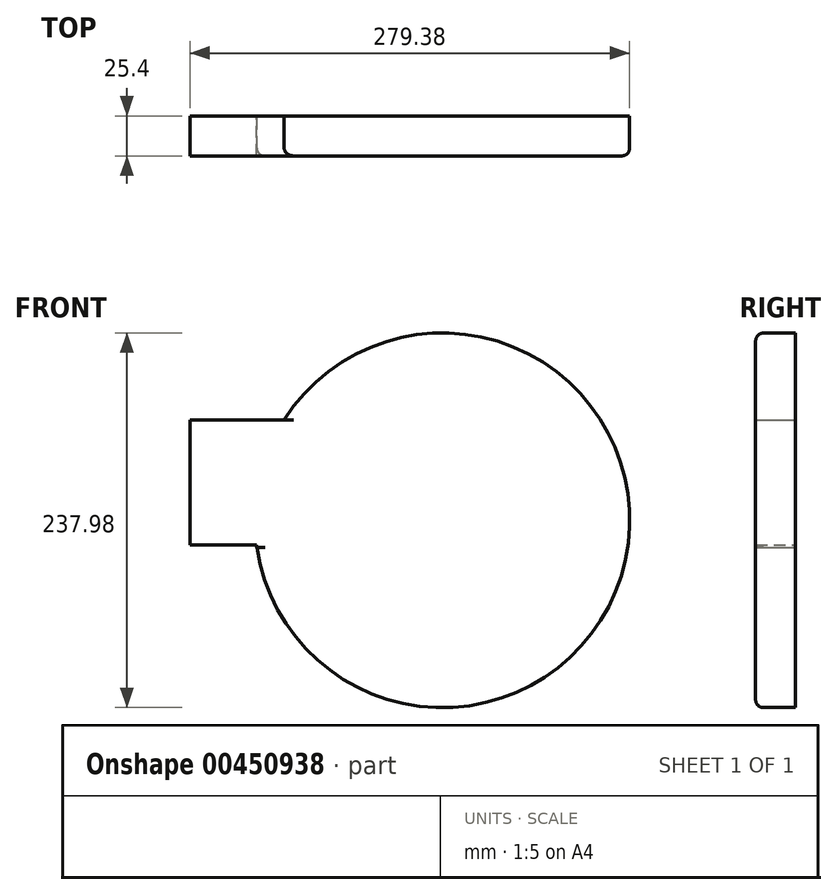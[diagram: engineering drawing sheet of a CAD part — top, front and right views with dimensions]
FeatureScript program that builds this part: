
annotation { "Feature Type Name" : "Feature", "Feature Type Description" : "" }
export const myFeature = defineFeature(function(context is Context, id is Id, definition is map)
    precondition{}
    {
        {
            var Q0;
            Q0=qCreatedBy(makeId("Front.planeOp"),FACE);
            var sketch = newSketch(context, id + "F0", { "sketchPlane" : qUnion([Q0])});
            skCircle(sketch, "E0", {"center": v(0, 0) * mm, "radius": 119 * mm});
            skLineSegment(sketch, "E1.bottom", {"start": v(-117.95, -15.75) * mm, "end": v(-160.4, -15.75) * mm});
            skLineSegment(sketch, "E1.top", {"start": v(-117.95, 63.74) * mm, "end": v(-160.4, 63.74) * mm});
            skLineSegment(sketch, "E1.left", {"start": v(-117.95, -15.75) * mm, "end": v(-117.95, 63.74) * mm});
            skLineSegment(sketch, "E1.right", {"start": v(-160.4, -15.75) * mm, "end": v(-160.4, 63.74) * mm});
            skLineSegment(sketch, "E2.bottom", {"start": v(-117.95, 63.74) * mm, "end": v(6.5, 63.74) * mm});
            skLineSegment(sketch, "E2.top", {"start": v(-117.95, -17.13) * mm, "end": v(6.5, -17.13) * mm});
            skLineSegment(sketch, "E2.left", {"start": v(-117.95, 63.74) * mm, "end": v(-117.95, -17.13) * mm});
            skLineSegment(sketch, "E2.right", {"start": v(6.5, 63.74) * mm, "end": v(6.5, -17.13) * mm});
            skSolve(sketch);
        }
        {
            var Q0;
            Q0 = qSketchRegion(id + "F0", true);
            var Q1;
            {var subQ5=sQuery(id+"F0.wireOp",EDGE,"E2.right");Q1=makeQuery(id+"F0.imprint","IMPRINT",FACE,{"disambiguationData":[TD([[makeQuery(id+"F0.imprint","IMPRINT",EDGE,{"derivedFrom":subQ5}),1.0]])]});}
            extrude(context, id + "F1", {"entities" : qUnion([Q0, Q1]), "depth" : 25.4 * mm});
        }
        {
            var Q0;
            Q0=makeQuery(id+"F1.opExtrude","CAP_EDGE",EDGE,{"disambiguationData":[OSD([sQuery(id+"F0.wireOp",EDGE,"E0")])],"isStart":false});
            fillet(context, id + "F2", {"entities" : qUnion([Q0]), "radius" : 5.08 * mm, "tangentPropagation" : true, "allowEdgeOverflow" : false});
        }
    });
